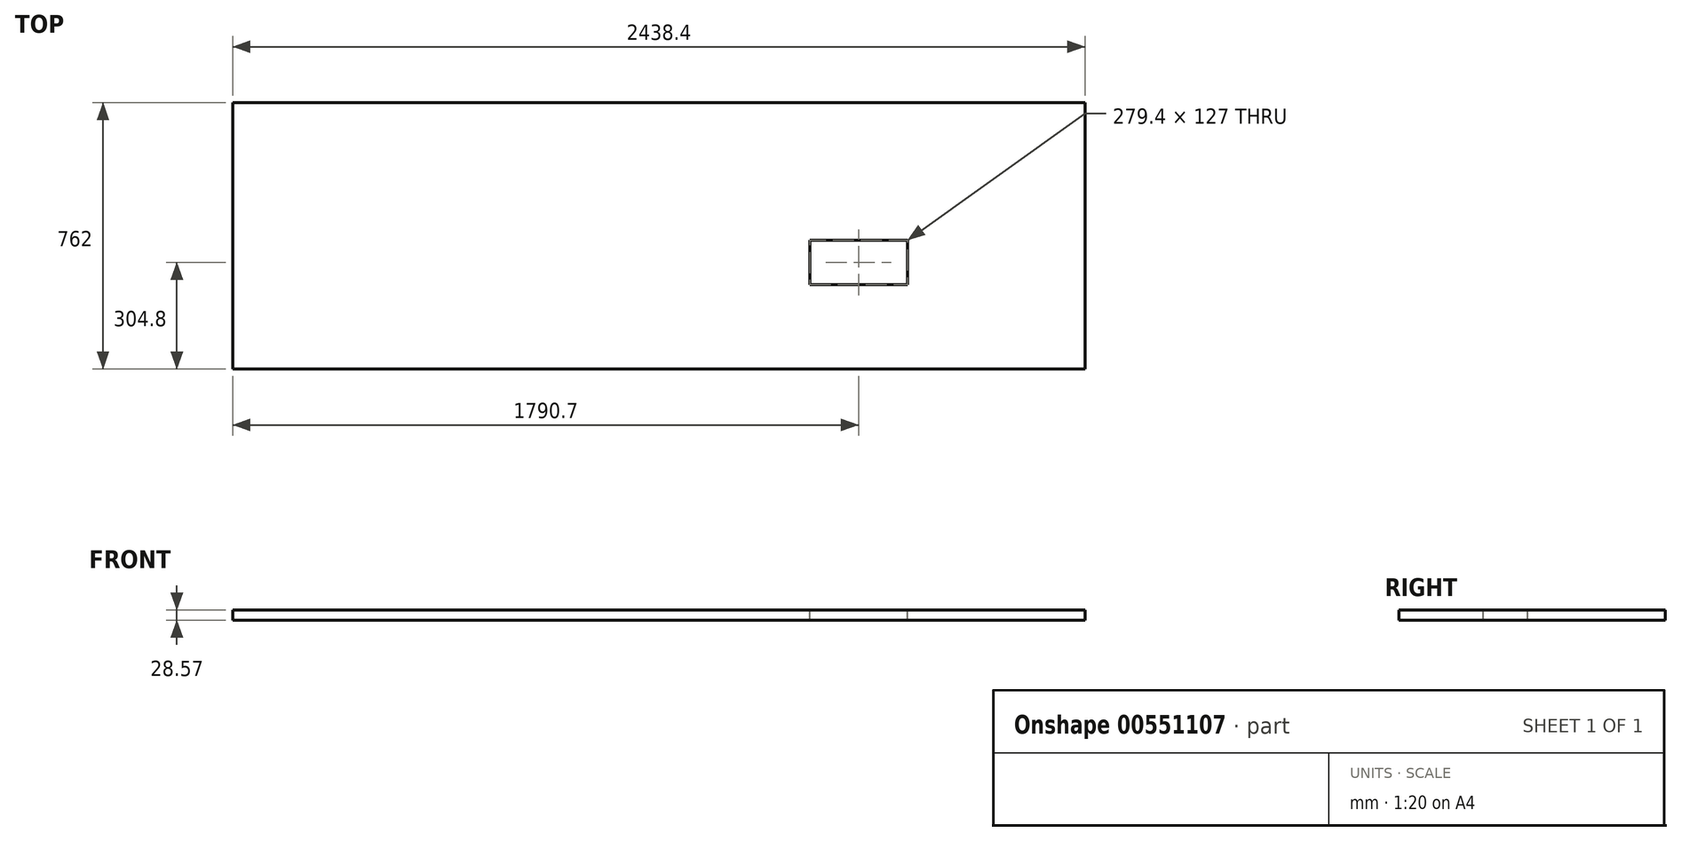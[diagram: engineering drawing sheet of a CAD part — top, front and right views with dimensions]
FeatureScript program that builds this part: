
annotation { "Feature Type Name" : "Feature", "Feature Type Description" : "" }
export const myFeature = defineFeature(function(context is Context, id is Id, definition is map)
    precondition{}
    {
        {
            var Q0;
            Q0=qCreatedBy(makeId("Top.planeOp"),FACE);
            var sketch = newSketch(context, id + "F0", { "sketchPlane" : qUnion([Q0])});
            skLineSegment(sketch, "E0.bottom", {"start": v(-1219.2, 381) * mm, "end": v(1219.2, 381) * mm});
            skLineSegment(sketch, "E0.top", {"start": v(-1219.2, -381) * mm, "end": v(1219.2, -381) * mm});
            skLineSegment(sketch, "E0.left", {"start": v(-1219.2, 381) * mm, "end": v(-1219.2, -381) * mm});
            skLineSegment(sketch, "E0.right", {"start": v(1219.2, 381) * mm, "end": v(1219.2, -381) * mm});
            skPoint(sketch, "E0.middle", {"position": v(0, 0) * mm});
            skSolve(sketch);
        }
        {
            var Q0;
            Q0=makeQuery(id+"F0.imprint","IMPRINT",FACE,{"disambiguationData":[TD([[makeQuery(id+"F0.imprint","IMPRINT",EDGE,{"derivedFrom":sQuery(id+"F0.wireOp",EDGE,"E0.bottom")}),-1.0]])]});
            extrude(context, id + "F1", {"entities" : qUnion([Q0]), "depth" : 28.57 * mm, "offsetDistance" : 25.4 * mm});
        }
        {
            var Q0;
            Q0=makeQuery(id+"F1.opExtrude","CAP_FACE",FACE,{"disambiguationData":[OSD([sQuery(id+"F0.wireOp",EDGE,"E0.bottom"),sQuery(id+"F0.wireOp",EDGE,"E0.top"),sQuery(id+"F0.wireOp",EDGE,"E0.left"),sQuery(id+"F0.wireOp",EDGE,"E0.right")])],"isStart":false});
            var sketch = newSketch(context, id + "F2", { "sketchPlane" : qUnion([Q0])});
            skLineSegment(sketch, "E1", {"start": v(1219.2, 0) * mm, "end": v(571.5, 0) * mm});
            skPoint(sketch, "E1.endSnap0", {"position": v(1219.2, 0) * mm});
            skLineSegment(sketch, "E2", {"start": v(571.5, 0) * mm, "end": v(571.5, -76.2) * mm});
            skLineSegment(sketch, "E3.bottom", {"start": v(431.8, -12.7) * mm, "end": v(711.2, -12.7) * mm});
            skLineSegment(sketch, "E3.top", {"start": v(431.8, -139.7) * mm, "end": v(711.2, -139.7) * mm});
            skLineSegment(sketch, "E3.left", {"start": v(431.8, -12.7) * mm, "end": v(431.8, -139.7) * mm});
            skLineSegment(sketch, "E3.right", {"start": v(711.2, -12.7) * mm, "end": v(711.2, -139.7) * mm});
            skPoint(sketch, "E3.middle", {"position": v(571.5, -76.2) * mm});
            skSolve(sketch);
        }
        {
            var Q0;
            Q0=makeQuery(id+"F2.imprint","IMPRINT",FACE,{"disambiguationData":[TD([[makeQuery(id+"F2.imprint","IMPRINT",EDGE,{"derivedFrom":sQuery(id+"F2.wireOp",EDGE,"E3.top")}),1.0]])]});
            extrude(context, id + "F3", {"entities" : qUnion([Q0]), "operationType" : NewBodyOperationType.REMOVE, "oppositeDirection" : true, "depth" : 31.75 * mm, "offsetDistance" : 25.4 * mm});
        }
    });
